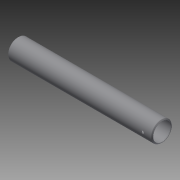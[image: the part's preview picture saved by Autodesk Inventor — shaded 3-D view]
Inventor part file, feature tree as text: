
AUTODESK INVENTOR PART (.ipt)
format: ipt  version: 2014 SP2 (Build 180246200, 246)  size: 143,872 bytes
history: native  units: in
note: dims shown in document units (in); Inventor stores cm internally (conversion verified against a paired STEP export)
features: other x42, sketch x2, revolve x1, extrude x1
ambient origin geometry x8: Origin, YZ Plane, XZ Plane, XY Plane, X Axis, Y Axis, Z Axis, Center Point
bodies: Solid1 (feature_tree)
feature tree (46):
  revolve  "Revolution1"  [1 undecoded]
  extrude  "Extrusion1"  [1 undecoded]
  other  "cp1_XY"
  other  "cp1_YZ"
  other  "cp1_ZX"
  other  "cp1_X"
  other  "cp1_Y"
  other  "cp1_Z"
  other  "cp1_Center"
  other  "cp2_XY"
  other  "cp2_YZ"
  other  "cp2_ZX"
  other  "cp2_X"
  other  "cp2_Y"
  other  "cp2_Z"
  other  "cp2_Center"
  other  "cp3_XY"
  other  "cp3_YZ"
  other  "cp3_ZX"
  other  "cp3_X"
  other  "cp3_Y"
  other  "cp3_Z"
  other  "cp3_Center"
  other  "cp4_XY"
  other  "cp4_YZ"
  other  "cp4_ZX"
  other  "cp4_X"
  other  "cp4_Y"
  other  "cp4_Z"
  other  "cp4_Center"
  other  "tube_front_XY"
  other  "tube_front_YZ"
  other  "tube_front_ZX"
  other  "tube_front_X"
  other  "tube_front_Y"
  other  "tube_front_Z"
  other  "tube_front_Center"
  other  "tube_rear_XY"
  other  "tube_rear_YZ"
  other  "tube_rear_ZX"
  other  "tube_rear_X"
  other  "tube_rear_Y"
  other  "tube_rear_Z"
  other  "tube_rear_Center"
  sketch  "Sketch_1"  dims[d0=360.0deg d1=0.4038in d2=0.0in]
  sketch  "Sketch_7"
note: 2 required parameter values undecoded (feature->parameter linkage not recoverable at this tier; creation-order binding heuristic only, values carry confidence <= 0.55)